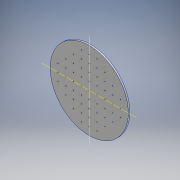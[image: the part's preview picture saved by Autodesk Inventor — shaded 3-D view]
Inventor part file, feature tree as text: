
AUTODESK INVENTOR PART (.ipt)
format: ipt  version: 2017 SP1 (Build 210196100, 196)  size: 163,840 bytes
history: native  units: mm
features: other x2, sketch x2, extrude x1, hole x1
ambient origin geometry x8: Origin, YZ Plane, XZ Plane, XY Plane, X Axis, Y Axis, Z Axis, Center Point
bodies: Solid1 (feature_tree)
feature tree (6):
  extrude  "Extrusion1"  Depth=10.0mm TaperAngle=0.0deg
  hole  "Hole1"  [1 undecoded]
  other  "Work Axis1"
  other  "Work Axis2"
  sketch  "Sketch1"  dims[d0=500.0mm d1=10.0mm d2=0.0mm]
  sketch  "Sketch2"  dims[d3=4.917mm d4=12.0mm d5=4.0mm d6=2.0mm d7=90.0deg d8=17.1mm d9=20.594885mm]
note: 1 required parameter value undecoded (feature->parameter linkage not recoverable at this tier; creation-order binding heuristic only, values carry confidence <= 0.55)
